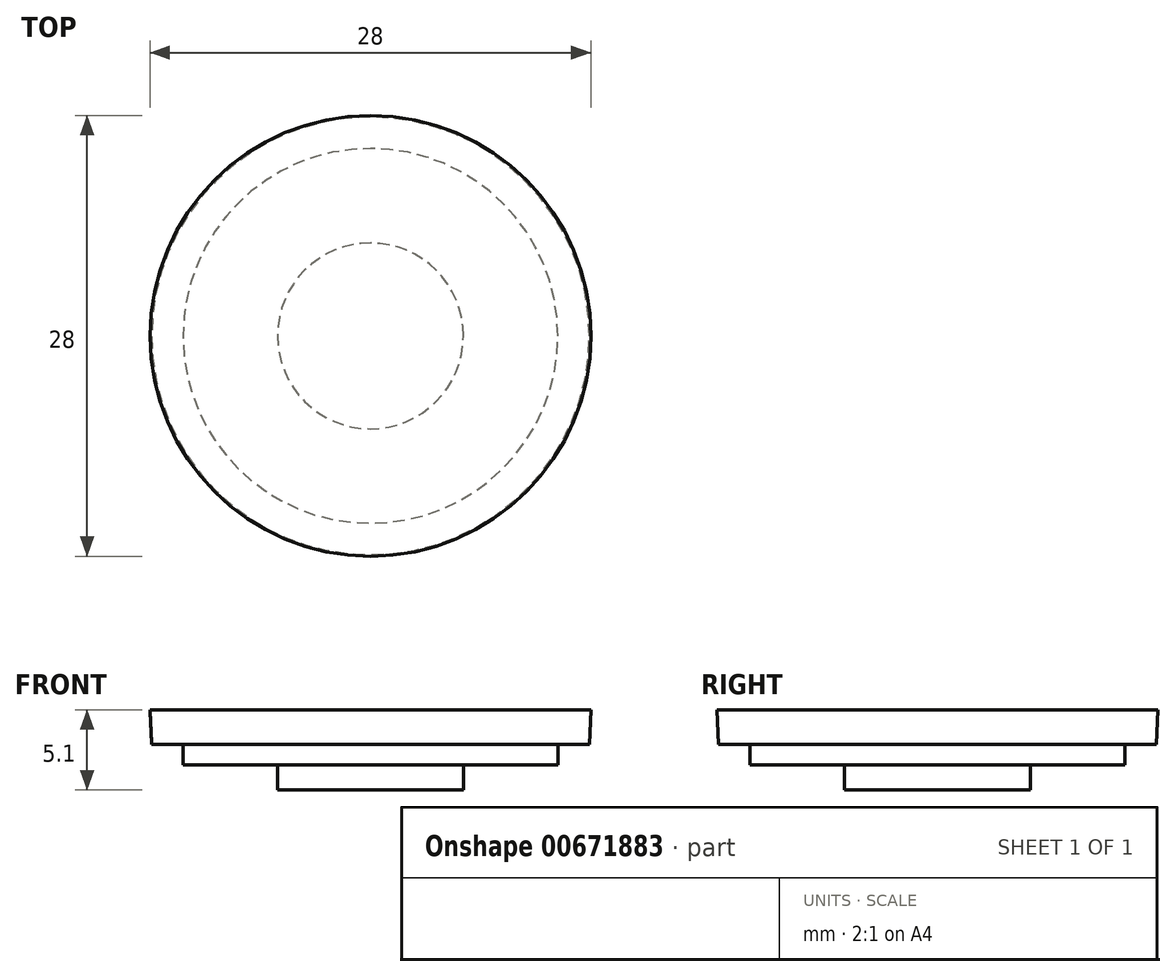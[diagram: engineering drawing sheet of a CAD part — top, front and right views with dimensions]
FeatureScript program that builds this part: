
annotation { "Feature Type Name" : "Feature", "Feature Type Description" : "" }
export const myFeature = defineFeature(function(context is Context, id is Id, definition is map)
    precondition{}
    {
        {
            var Q0;
            Q0=qCreatedBy(makeId("Front.planeOp"),FACE);
            var sketch = newSketch(context, id + "F0", { "sketchPlane" : qUnion([Q0])});
            skLineSegment(sketch, "E0", {"start": v(0, 0) * mm, "end": v(14, 0) * mm});
            skLineSegment(sketch, "E1", {"start": v(14, 0) * mm, "end": v(13.9, -2.2) * mm});
            skLineSegment(sketch, "E2", {"start": v(13.9, -2.2) * mm, "end": v(11.9, -2.2) * mm});
            skLineSegment(sketch, "E3", {"start": v(11.9, -2.2) * mm, "end": v(11.9, -3.5) * mm});
            skLineSegment(sketch, "E4", {"start": v(11.9, -3.5) * mm, "end": v(5.9, -3.5) * mm});
            skLineSegment(sketch, "E5", {"start": v(5.9, -3.5) * mm, "end": v(5.9, -5.1) * mm});
            skLineSegment(sketch, "E6", {"start": v(5.9, -5.1) * mm, "end": v(0, -5.1) * mm});
            skLineSegment(sketch, "E7", {"start": v(0, -5.1) * mm, "end": v(0, 0) * mm});
            skSolve(sketch);
        }
        {
            var Q0;
            Q0=makeQuery(id+"F0.imprint","IMPRINT",FACE,{"disambiguationData":[TD([[makeQuery(id+"F0.imprint","IMPRINT",EDGE,{"derivedFrom":sQuery(id+"F0.wireOp",EDGE,"E0")}),-1.0]])]});
            var Q1;
            Q1=sQuery(id+"F0.wireOp",EDGE,"E7");
            revolve(context, id + "F1", {"entities" : qUnion([Q0]), "axis" : qUnion([Q1]), "revolveType" : RevolveType.FULL});
        }
    });
